# Revit family: 55-9906-CA-CL
name_source: partatom
category: Luminarias
revit_build: Autodesk Revit 2017 (Build: 20160225_1515(x64)
units: mm (PartAtom-declared; Revit-internal decimal feet)

## family parameters
Compartido = Sí
Corte con vacíos al cargar = No
Cota de conector redondo = Diámetro de uso
Número OmniClass = 23.80.70.00
Origen de luz = No
Punto de cálculo de habitación = No
Se basa en plano de trabajo = No
Siempre vertical = Sí
Tipo de pieza = Normal
Título OmniClass = Lighting

## types (1)
- 55-9906-CA-CL
    Acabado = Pulido, Negro, Transparente
    CRI = 80
    Catálogo = Outdoor
    CodigoGubimclass = 50.60.50.20
    CodigoOmniclass = 21-04 50 40
    CodigoUniclass2015 = EF_70_80
    CodigoUniformat2010 = D5040
    DescripcionGubimclass = Iluminación interior
    DescripcionOmniclass = Lighting
    DescripcionUniclass2015 = Lighting
    DescripcionUniformat2010 = Lighting
    EAN13 = 8435381439958
    Eficiencia energética = LED A++
    Etiqueta V/f = 100-240V/50-60Hz
    Fabricante = LEDS C4
    Familia = Gea Cob LED Aluminium ø125mm Structure
    FechaVersion = Julio 2020
    Ficha = http://files.leds-c4.com
    Fotometría = http://files.leds-c4.com
    Fuente de luz = 1xLED 9 995.00 lm
    IK = IK10
    IMC = http://files.leds-c4.com
    IP = IP65/IP67
    IfcExportAs = IfcLightFixture
    IfcExportType = NOTDEFINED
    Imagen web = http://files.leds-c4.com
    LDT = http://files.leds-c4.com
    Lumenes reales (lm) = 869
    Material = Acero inoxidable AISI 316, Aluminio, Cristal
    Peso neto (KG) = 1
    Pluma comercial = http://files.leds-c4.com
    Producto descatalogado = Catalogado ES
    Rayo de luz = EXTRA SPOT, 60º
    Referencia = 55-9906-CA-CL
    Temperatura color led (K) = Blanco cálido - 3000K
    Tender text (Castellano) = LEDS C4
Gea Cob LED Aluminium ø125mm Structure
55-9906-CA-CL

Empotrado de suelo de uso exterior para iluminar hacia arriba. 

Partes eléctricas situadas en un compartimento estanco interior, aisladas del compartimiento donde hay la regleta para hacer la conexión. Soporta un peso estático de hasta 1.800 Kg y el paso ocasional de vehículos a baja velocidad. Incluye 2 accesorios antideslumbrantes. Incluye 2 reflectores. Incluye caja de empotrar. Apto para instalar en ambientes con atmósfera marina. Incluye 2 salidas de cable para facilitar la instalación en cadena. Temperatura máxima en la superficie de la luminaria inferior a 40ºC. Fuente de luz orientable. Material estructura: Acero inoxidable AISI 316, Aluminio. Acabado estructura: Pulido, Negro. Material difusor: Cristal. Acabado difusor: Transparente. Protección contra los rayos ultravioleta. Garantía: 5 Años.

Peso neto del producto (Kg): 1.000
Anchura o diámetro del producto (mm): 125
Salida del producto (mm): 133

Clase 1. Prueba hilo incandescente: 850. IP: IP65/IP67. IK: IK10. LED. Nº de portalámparas o Leds: 1. Marca del LED: CREE. Marca del Driver: EAGLERISE. Potencia máxima de la fuente de luz: 9W. Temperatura de color: Blanco cálido - 3000K. Índice de reproducción cromática: 80. Steps Mac Adam: 2. Diámetro máximo de la bombilla que admite la luminaria: 50.000h L80B20. UGR:  9.2. Riesgo fotobiológico: RG1. Flujo real (lm): 869. Flujo nominal (lm): 995. Lm/W reales: 83. Rango de voltaje/frecuencia: 100-240 VAC. Voltaje: 18. Equipo incluido: Si, electrónico. Equipo multivoltaje incluido. Potencia total: 10.5. Factor de potencia: 0.92.
    Tender text (English) = LEDS C4
Gea Cob LED Aluminium ø125mm Structure
55-9906-CA-CL

Floor recessed for outdoor use. 

For uplighting. Electronic components are in a sealed internal compartment, completely separate from the compartment where the connection terminals are located. The unit will withstand a static weight of 1,800 Kg and the occasional transit of slow-moving vehicles. Includes 2 anti-glare accessories. Includes 2 reflectors. Includes flush-mounting box. Suitable for installation in marine environments. Includes 2 cable outlets to facilitate chain mounting. Maximum light surface temperature below 40ºC. Adjustable light source. Structure material: Stainless steel AISI316, Aluminium. Structure finish: Polished, Black. Diffuser material: Glass. Diffuser finish: Transparent. UV protection. Warranty: 5 Years.

Product net weight (Kg): 1.000
Product width or diameter (mm): 125
Product aperture (mm): 133

Class 1. Glow wire test: 850. IP: IP65/IP67. IK: IK10. LED. No. of lampholders or LEDs: 1. LED brand: CREE. Driver brand: EAGLERISE. Maximum power of light source: 9W. Colour temperature: LED warm-white 3000K. Colour rendering index: 80. MacAdam Steps: 2. Maximum diameter of luminaire bulb: 50.000h L80B20. UGR:  9.2. Photobiological risk: RG1. Real flux (lm): 869. Nominal flux (lm): 995. Lm/Real W: 83. Voltage and frequency range: 100-240 VAC. Voltage: 18. Gear included: Yes, electronic. Multi-voltage gear included. Total power: 10.5. Power factor: 0.92.
    Tipo = Empotrable de suelo
    Vatios (W) = 10.5
    Versión = v1
